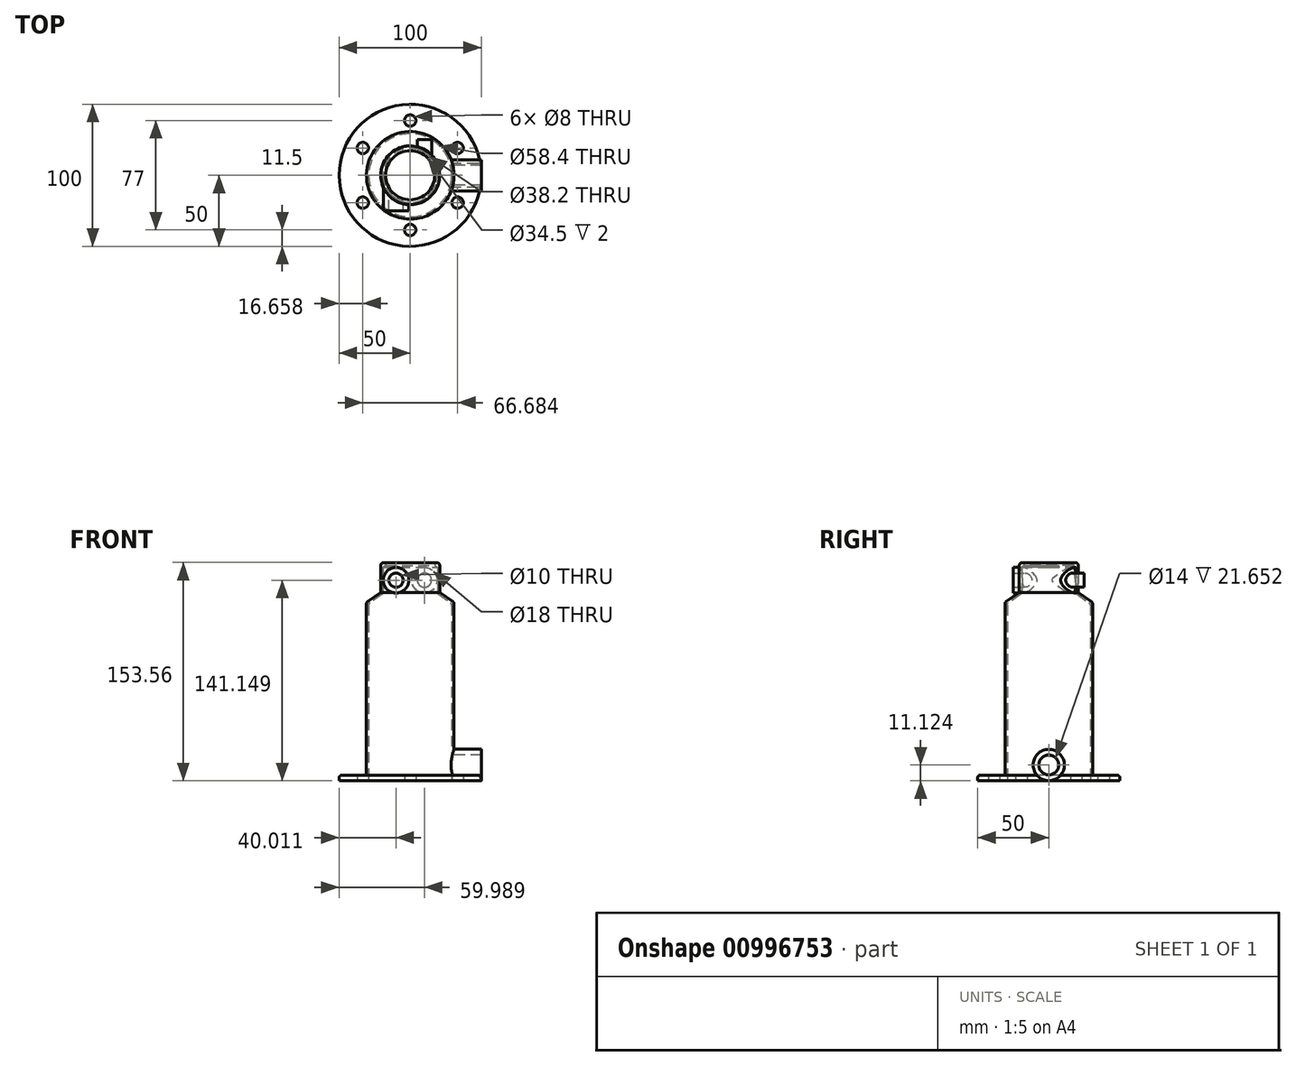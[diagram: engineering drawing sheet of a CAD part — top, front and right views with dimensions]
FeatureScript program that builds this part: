
annotation { "Feature Type Name" : "Feature", "Feature Type Description" : "" }
export const myFeature = defineFeature(function(context is Context, id is Id, definition is map)
    precondition{}
    {
        {
            var Q0;
            Q0=qCreatedBy(makeId("Top.planeOp"),FACE);
            var sketch = newSketch(context, id + "F0", { "sketchPlane" : qUnion([Q0])});
            skCircle(sketch, "E0", {"center": v(0, 0) * mm, "radius": 50 * mm});
            skCircle(sketch, "E1", {"center": v(0, 0) * mm, "radius": 29.2 * mm});
            skCircle(sketch, "E2", {"center": v(0, -38.5) * mm, "radius": 4 * mm});
            skCircle(sketch, "E3.1.0", {"center": v(33.34, -19.25) * mm, "radius": 4 * mm});
            skCircle(sketch, "E3.2.0", {"center": v(33.34, 19.25) * mm, "radius": 4 * mm});
            skCircle(sketch, "E3.3.0", {"center": v(0, 38.5) * mm, "radius": 4 * mm});
            skCircle(sketch, "E3.4.0", {"center": v(-33.34, 19.25) * mm, "radius": 4 * mm});
            skCircle(sketch, "E3.5.0", {"center": v(-33.34, -19.25) * mm, "radius": 4 * mm});
            skSolve(sketch);
        }
        {
            var Q0;
            Q0=qCreatedBy(makeId("Front.planeOp"),FACE);
            var sketch = newSketch(context, id + "F1", { "sketchPlane" : qUnion([Q0])});
            skLineSegment(sketch, "E4", {"start": v(0, 0) * mm, "end": v(0, 160.73) * mm});
            skLineSegment(sketch, "E5", {"start": v(-29.2, 0) * mm, "end": v(-29.2, 124.67) * mm});
            skLineSegment(sketch, "E6", {"start": v(-29.2, 124.67) * mm, "end": v(-19.1, 131.74) * mm});
            skLineSegment(sketch, "E7", {"start": v(-19.1, 131.74) * mm, "end": v(-19.1, 150.26) * mm});
            skLineSegment(sketch, "E8.0", {"start": v(-20.7, 153.56) * mm, "end": v(-17.25, 153.56) * mm});
            skLineSegment(sketch, "E8.1", {"start": v(-20.7, 132.57) * mm, "end": v(-20.7, 153.56) * mm});
            skLineSegment(sketch, "E8.2", {"start": v(-30.8, 125.5) * mm, "end": v(-20.7, 132.57) * mm});
            skLineSegment(sketch, "E8.3", {"start": v(-30.8, 0) * mm, "end": v(-30.8, 125.5) * mm});
            skLineSegment(sketch, "E9", {"start": v(-30.8, 0) * mm, "end": v(-29.2, 0) * mm});
            skLineSegment(sketch, "E10", {"start": v(-19.1, 150.26) * mm, "end": v(-17.25, 151.56) * mm});
            skLineSegment(sketch, "E11", {"start": v(-17.25, 151.56) * mm, "end": v(-17.25, 153.56) * mm});
            skSolve(sketch);
        }
        {
            var Q0;
            Q0 = qSketchRegion(id + "F0", true);
            extrude(context, id + "F2", {"entities" : qUnion([Q0]), "depth" : 4 * mm, "offsetDistance" : 25 * mm});
        }
        {
            var Q0;
            Q0 = qSketchRegion(id + "F1", true);
            var Q1;
            Q1=sQuery(id+"F1.wireOp",EDGE,"E4");
            revolve(context, id + "F3", {"operationType" : NewBodyOperationType.ADD, "surfaceOperationType" : NewSurfaceOperationType.NEW, "entities" : qUnion([Q0]), "axis" : qUnion([Q1]), "revolveType" : RevolveType.FULL});
        }
        {
            var Q0;
            Q0=qCreatedBy(makeId("Front.planeOp"),FACE);
            var sketch = newSketch(context, id + "F4", { "sketchPlane" : qUnion([Q0])});
            skCircle(sketch, "E12", {"center": v(-9.99, 141.15) * mm, "radius": 5 * mm});
            skCircle(sketch, "E13", {"center": v(-9.99, 141.15) * mm, "radius": 9 * mm});
            skCircle(sketch, "E14.MirrorC", {"center": v(9.99, 141.15) * mm, "radius": 5 * mm});
            skCircle(sketch, "E15.MirrorC", {"center": v(9.99, 141.15) * mm, "radius": 9 * mm});
            skSolve(sketch);
        }
        {
            var Q0;
            Q0=makeQuery(id+"F4.imprint","IMPRINT",FACE,{"disambiguationData":[TD([[makeQuery(id+"F4.imprint","IMPRINT",EDGE,{"derivedFrom":sQuery(id+"F4.wireOp",EDGE,"E12")}),1.0]])]});
            var Q1;
            Q1=sQuery(id+"F4.wireOp",EDGE,"E12");
            extrude(context, id + "F5", {"entities" : qUnion([Q0]), "operationType" : NewBodyOperationType.REMOVE, "surfaceEntities" : qUnion([Q1]), "depth" : 25 * mm, "offsetDistance" : 25 * mm});
        }
        {
            var Q0;
            Q0=makeQuery(id+"F4.imprint","IMPRINT",FACE,{"disambiguationData":[TD([[makeQuery(id+"F4.imprint","IMPRINT",EDGE,{"derivedFrom":sQuery(id+"F4.wireOp",EDGE,"E12")}),-1.0]])]});
            extrude(context, id + "F6", {"entities" : qUnion([Q0]), "operationType" : NewBodyOperationType.ADD, "depth" : 25 * mm, "offsetDistance" : 25 * mm});
        }
        {
            var Q0;
            Q0=makeQuery(id+"F4.imprint","IMPRINT",FACE,{"disambiguationData":[TD([[makeQuery(id+"F4.imprint","IMPRINT",EDGE,{"derivedFrom":sQuery(id+"F4.wireOp",EDGE,"E14.MirrorC")}),-1.0]])]});
            extrude(context, id + "F7", {"entities" : qUnion([Q0]), "operationType" : NewBodyOperationType.REMOVE, "oppositeDirection" : true, "depth" : 25 * mm, "offsetDistance" : 25 * mm});
        }
        {
            var Q0;
            Q0=makeQuery(id+"F4.imprint","IMPRINT",FACE,{"disambiguationData":[TD([[makeQuery(id+"F4.imprint","IMPRINT",EDGE,{"derivedFrom":sQuery(id+"F4.wireOp",EDGE,"E14.MirrorC")}),1.0]])]});
            extrude(context, id + "F8", {"entities" : qUnion([Q0]), "operationType" : NewBodyOperationType.ADD, "oppositeDirection" : true, "depth" : 25 * mm, "offsetDistance" : 25 * mm});
        }
        {
            var Q0;
            Q0=qCreatedBy(makeId("Front.planeOp"),FACE);
            var sketch = newSketch(context, id + "F9", { "sketchPlane" : qUnion([Q0])});
            skLineSegment(sketch, "E16.bottom", {"start": v(-19.1, 150.23) * mm, "end": v(-0.79, 150.23) * mm});
            skLineSegment(sketch, "E16.top", {"start": v(-19.1, 131.47) * mm, "end": v(-0.79, 131.47) * mm});
            skLineSegment(sketch, "E16.left", {"start": v(-19.1, 150.23) * mm, "end": v(-19.1, 131.47) * mm});
            skLineSegment(sketch, "E16.right", {"start": v(-0.79, 150.23) * mm, "end": v(-0.79, 131.47) * mm});
            skLineSegment(sketch, "E17", {"start": v(0, 0) * mm, "end": v(0, 165.48) * mm});
            skLineSegment(sketch, "E18.bottom", {"start": v(-29.2, 0) * mm, "end": v(0, 0) * mm});
            skLineSegment(sketch, "E18.top", {"start": v(-29.2, 27.48) * mm, "end": v(0, 27.48) * mm});
            skLineSegment(sketch, "E18.left", {"start": v(-29.2, 0) * mm, "end": v(-29.2, 27.48) * mm});
            skLineSegment(sketch, "E18.right", {"start": v(0, 0) * mm, "end": v(0, 27.48) * mm});
            skSolve(sketch);
        }
        {
            var Q0;
            Q0=qCreatedBy(makeId("Right.planeOp"),FACE);
            var sketch = newSketch(context, id + "F10", { "sketchPlane" : qUnion([Q0])});
            skCircle(sketch, "E19", {"center": v(0, 11.12) * mm, "radius": 7 * mm});
            skCircle(sketch, "E20", {"center": v(0, 11.12) * mm, "radius": 11 * mm});
            skSolve(sketch);
        }
        {
            var Q0;
            Q0=makeQuery(id+"F10.imprint","IMPRINT",FACE,{"disambiguationData":[TD([[makeQuery(id+"F10.imprint","IMPRINT",EDGE,{"derivedFrom":sQuery(id+"F10.wireOp",EDGE,"E19")}),1.0]])]});
            var Q1;
            Q1=sQuery(id+"F10.wireOp",EDGE,"E19");
            extrude(context, id + "F11", {"entities" : qUnion([Q0]), "operationType" : NewBodyOperationType.REMOVE, "surfaceEntities" : qUnion([Q1]), "depth" : 50.5 * mm, "offsetDistance" : 25 * mm});
        }
        {
            var Q0;
            Q0=makeQuery(id+"F10.imprint","IMPRINT",FACE,{"disambiguationData":[TD([[makeQuery(id+"F10.imprint","IMPRINT",EDGE,{"derivedFrom":sQuery(id+"F10.wireOp",EDGE,"E19")}),-1.0]])]});
            extrude(context, id + "F12", {"entities" : qUnion([Q0]), "operationType" : NewBodyOperationType.ADD, "depth" : 50 * mm, "offsetDistance" : 25 * mm});
        }
        {
            var Q0;
            Q0=makeQuery(id+"F9.imprint","IMPRINT",FACE,{"disambiguationData":[TD([[makeQuery(id+"F9.imprint","IMPRINT",EDGE,{"derivedFrom":sQuery(id+"F9.wireOp",EDGE,"E16.bottom")}),-1.0]])]});
            var Q1;
            Q1=makeQuery(id+"F9.imprint","IMPRINT",FACE,{"disambiguationData":[TD([[makeQuery(id+"F9.imprint","IMPRINT",EDGE,{"derivedFrom":sQuery(id+"F9.wireOp",EDGE,"E18.bottom")}),1.0]])]});
            var Q2;
            Q2=sQuery(id+"F9.wireOp",EDGE,"E16.top");
            var Q3;
            Q3=sQuery(id+"F9.wireOp",EDGE,"E16.left");
            var Q4;
            Q4=sQuery(id+"F9.wireOp",EDGE,"E16.right");
            var Q5;
            Q5=sQuery(id+"F9.wireOp",EDGE,"E16.bottom");
            var Q6;
            Q6=sQuery(id+"F9.wireOp",EDGE,"E17");
            revolve(context, id + "F13", {"operationType" : NewBodyOperationType.REMOVE, "surfaceOperationType" : NewSurfaceOperationType.NEW, "entities" : qUnion([Q0, Q1]), "surfaceEntities" : qUnion([Q2, Q3, Q4, Q5]), "axis" : qUnion([Q6]), "revolveType" : RevolveType.FULL, "oppositeDirection" : true});
        }
        {
            var Q0;
            Q0=makeQuery(id+"F2.opExtrude","CAP_EDGE",EDGE,{"disambiguationData":[OSD([sQuery(id+"F0.wireOp",EDGE,"E0")])],"isStart":false});
            var Q1;
            Q1=makeQuery(id+"F3.opRevolve","SWEPT_EDGE",EDGE,{"disambiguationData":[OSD([sQuery(id+"F1.wireOp",EDGE,"E8.2"),sQuery(id+"F1.wireOp",EDGE,"E8.3")])]});
            var Q2;
            Q2=makeQuery(id+"F3.opRevolve","SWEPT_EDGE",EDGE,{"disambiguationData":[OSD([sQuery(id+"F1.wireOp",EDGE,"E8.0"),sQuery(id+"F1.wireOp",EDGE,"E8.1")])]});
            var Q3;
            Q3=makeQuery(id+"F3.opRevolve","SWEPT_EDGE",EDGE,{"disambiguationData":[OSD([sQuery(id+"F1.wireOp",EDGE,"E6"),sQuery(id+"F1.wireOp",EDGE,"E7")])]});
            var Q4;
            Q4=makeQuery(id+"F3.opRevolve","SWEPT_EDGE",EDGE,{"disambiguationData":[OSD([sQuery(id+"F1.wireOp",EDGE,"E5"),sQuery(id+"F1.wireOp",EDGE,"E6")])]});
            fillet(context, id + "F14", {"entities" : qUnion([Q0, Q1, Q2, Q3, Q4]), "radius" : 2 * mm, "tangentPropagation" : true, "allowEdgeOverflow" : false});
        }
    });
